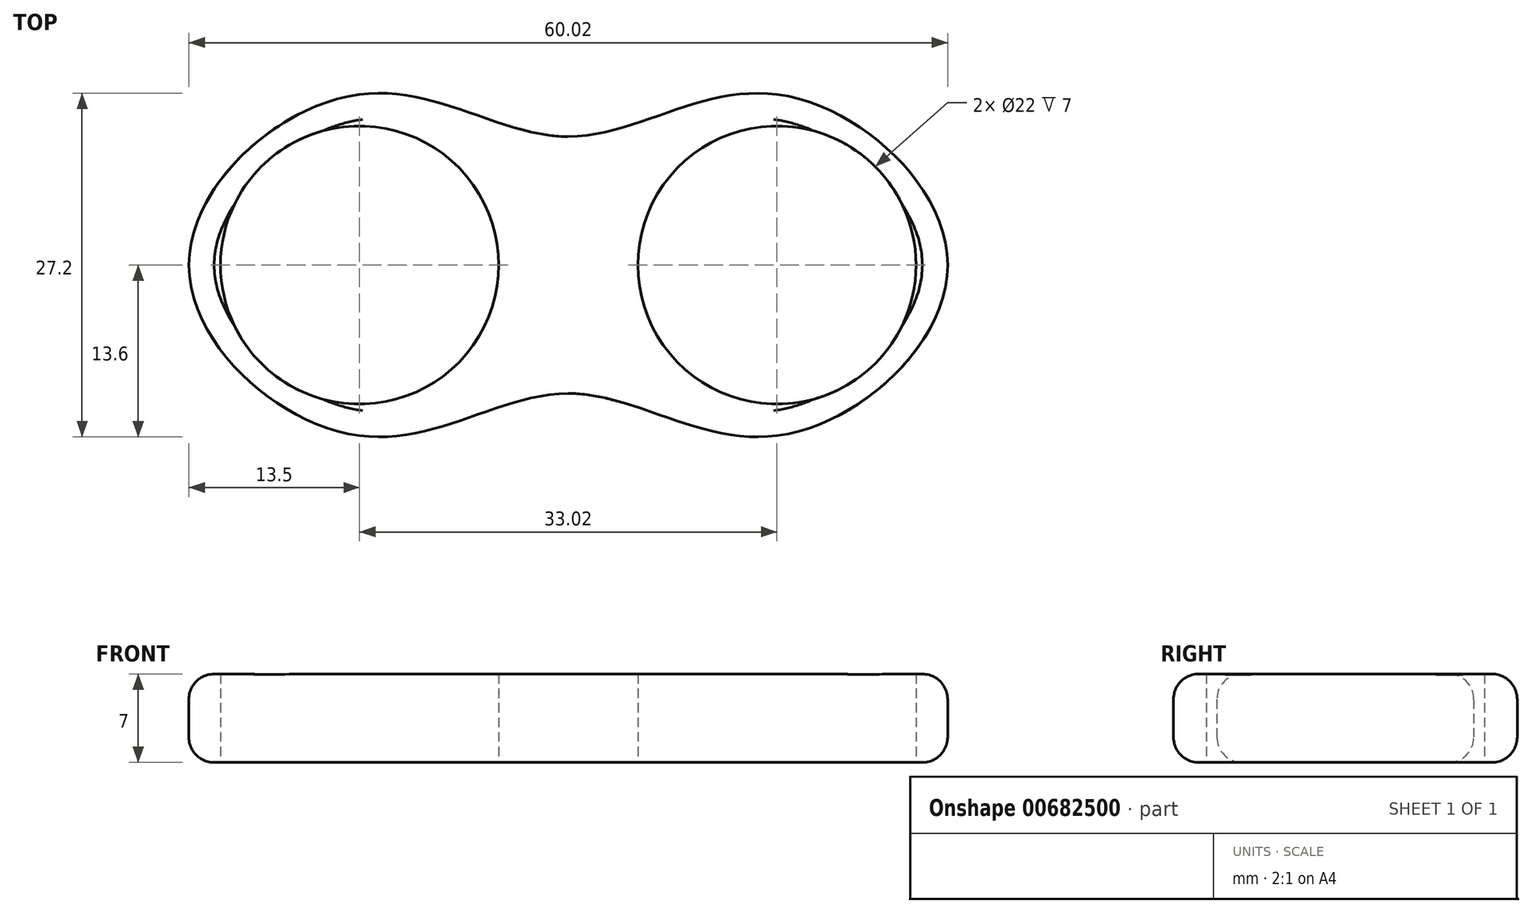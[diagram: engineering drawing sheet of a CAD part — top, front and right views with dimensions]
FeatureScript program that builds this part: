
annotation { "Feature Type Name" : "Feature", "Feature Type Description" : "" }
export const myFeature = defineFeature(function(context is Context, id is Id, definition is map)
    precondition{}
    {
        {
            var Q0;
            Q0=qCreatedBy(makeId("Top.planeOp"),FACE);
            var sketch = newSketch(context, id + "F0", { "sketchPlane" : qUnion([Q0])});
            skLineSegment(sketch, "E0", {"start": v(0, 0) * mm, "end": v(0, 10.16) * mm});
            skLineSegment(sketch, "E1", {"start": v(0, 0) * mm, "end": v(0, -10.16) * mm});
            skLineSegment(sketch, "E2", {"start": v(0, 0) * mm, "end": v(16.51, 0) * mm});
            skLineSegment(sketch, "E3", {"start": v(0, 0) * mm, "end": v(-16.51, 0) * mm});
            skCircle(sketch, "E4", {"center": v(-16.51, 0) * mm, "radius": 11 * mm});
            skCircle(sketch, "E5", {"center": v(16.51, 0) * mm, "radius": 11 * mm});
            skCircle(sketch, "E6", {"center": v(-16.51, 0) * mm, "radius": 13.5 * mm});
            skCircle(sketch, "E7", {"center": v(16.51, 0) * mm, "radius": 13.5 * mm});
            skLineSegment(sketch, "E8", {"start": v(-16.51, 0) * mm, "end": v(-16.51, 13.5) * mm});
            skLineSegment(sketch, "E9", {"start": v(-16.51, 0) * mm, "end": v(-30.01, 0) * mm});
            skLineSegment(sketch, "E10", {"start": v(-16.51, 0) * mm, "end": v(-16.51, -13.5) * mm});
            skLineSegment(sketch, "E11", {"start": v(16.51, 0) * mm, "end": v(16.51, -13.5) * mm});
            skLineSegment(sketch, "E12", {"start": v(16.51, 0) * mm, "end": v(30.01, 0) * mm});
            skLineSegment(sketch, "E13", {"start": v(16.51, 0) * mm, "end": v(16.51, 13.5) * mm});
            skFitSpline(sketch, "E14", {"points": [v(0, 10.16) * mm, v(-16.51, 13.5) * mm, v(-30.01, 0) * mm, v(-16.51, -13.5) * mm, v(0, -10.16) * mm, v(16.51, -13.5) * mm, v(30.01, 0) * mm, v(16.51, 13.5) * mm, v(0, 10.16) * mm]});
            skSolve(sketch);
        }
        {
            var Q0;
            {var subQ0=sQuery(id+"F0.wireOp",EDGE,"E0");Q0=makeQuery(id+"F0.imprint","IMPRINT",FACE,{"disambiguationData":[TD([[makeQuery(id+"F0.imprint","IMPRINT",EDGE,{"derivedFrom":subQ0}),-1.0]])]});}
            var Q1;
            {var subQ0=sQuery(id+"F0.wireOp",EDGE,"E0");Q1=makeQuery(id+"F0.imprint","IMPRINT",FACE,{"disambiguationData":[TD([[makeQuery(id+"F0.imprint","IMPRINT",EDGE,{"derivedFrom":subQ0}),1.0]])]});}
            var Q2;
            {var subQ0=sQuery(id+"F0.wireOp",EDGE,"E1");Q2=makeQuery(id+"F0.imprint","IMPRINT",FACE,{"disambiguationData":[TD([[makeQuery(id+"F0.imprint","IMPRINT",EDGE,{"derivedFrom":subQ0}),-1.0]])]});}
            var Q3;
            {var subQ0=sQuery(id+"F0.wireOp",EDGE,"E1");Q3=makeQuery(id+"F0.imprint","IMPRINT",FACE,{"disambiguationData":[TD([[makeQuery(id+"F0.imprint","IMPRINT",EDGE,{"derivedFrom":subQ0}),1.0]])]});}
            var Q4;
            {var subQ0=sQuery(id+"F0.wireOp",EDGE,"E7");var subQ1=sQuery(id+"F0.wireOp",EDGE,"E2");var subQ2=makeQuery(id+"F0.imprint","INTERSECT",VERTEX,{"derivedFrom":[subQ1,subQ0]});Q4=makeQuery(id+"F0.imprint","IMPRINT",FACE,{"disambiguationData":[TD([[makeQuery(id+"F0.imprint","IMPRINT",EDGE,{"disambiguationData":[TD([[subQ2,-1.0]])],"derivedFrom":subQ1}),-1.0]])]});}
            var Q5;
            {var subQ0=sQuery(id+"F0.wireOp",EDGE,"E7");var subQ1=sQuery(id+"F0.wireOp",EDGE,"E2");var subQ2=makeQuery(id+"F0.imprint","INTERSECT",VERTEX,{"derivedFrom":[subQ1,subQ0]});Q5=makeQuery(id+"F0.imprint","IMPRINT",FACE,{"disambiguationData":[TD([[makeQuery(id+"F0.imprint","IMPRINT",EDGE,{"disambiguationData":[TD([[subQ2,-1.0]])],"derivedFrom":subQ1}),1.0]])]});}
            var Q6;
            {var subQ0=sQuery(id+"F0.wireOp",EDGE,"E6");var subQ1=sQuery(id+"F0.wireOp",EDGE,"E3");var subQ2=makeQuery(id+"F0.imprint","INTERSECT",VERTEX,{"derivedFrom":[subQ1,subQ0]});Q6=makeQuery(id+"F0.imprint","IMPRINT",FACE,{"disambiguationData":[TD([[makeQuery(id+"F0.imprint","IMPRINT",EDGE,{"disambiguationData":[TD([[subQ2,-1.0]])],"derivedFrom":subQ1}),-1.0]])]});}
            var Q7;
            {var subQ0=sQuery(id+"F0.wireOp",EDGE,"E6");var subQ1=sQuery(id+"F0.wireOp",EDGE,"E3");var subQ2=makeQuery(id+"F0.imprint","INTERSECT",VERTEX,{"derivedFrom":[subQ1,subQ0]});Q7=makeQuery(id+"F0.imprint","IMPRINT",FACE,{"disambiguationData":[TD([[makeQuery(id+"F0.imprint","IMPRINT",EDGE,{"disambiguationData":[TD([[subQ2,-1.0]])],"derivedFrom":subQ1}),1.0]])]});}
            var Q8;
            {var subQ0=sQuery(id+"F0.wireOp",EDGE,"E9");var subQ1=sQuery(id+"F0.wireOp",EDGE,"E4");var subQ2=makeQuery(id+"F0.imprint","INTERSECT",VERTEX,{"derivedFrom":[subQ1,subQ0]});Q8=makeQuery(id+"F0.imprint","IMPRINT",FACE,{"disambiguationData":[TD([[makeQuery(id+"F0.imprint","IMPRINT",EDGE,{"disambiguationData":[TD([[subQ2,-1.0]])],"derivedFrom":subQ1}),-1.0]])]});}
            var Q9;
            {var subQ0=sQuery(id+"F0.wireOp",EDGE,"E8");var subQ1=sQuery(id+"F0.wireOp",EDGE,"E4");var subQ2=makeQuery(id+"F0.imprint","INTERSECT",VERTEX,{"derivedFrom":[subQ1,subQ0]});Q9=makeQuery(id+"F0.imprint","IMPRINT",FACE,{"disambiguationData":[TD([[makeQuery(id+"F0.imprint","IMPRINT",EDGE,{"disambiguationData":[TD([[subQ2,-1.0]])],"derivedFrom":subQ1}),-1.0]])]});}
            var Q10;
            {var subQ0=sQuery(id+"F0.wireOp",EDGE,"E13");var subQ1=sQuery(id+"F0.wireOp",EDGE,"E5");var subQ2=makeQuery(id+"F0.imprint","INTERSECT",VERTEX,{"derivedFrom":[subQ1,subQ0]});Q10=makeQuery(id+"F0.imprint","IMPRINT",FACE,{"disambiguationData":[TD([[makeQuery(id+"F0.imprint","IMPRINT",EDGE,{"disambiguationData":[TD([[subQ2,1.0]])],"derivedFrom":subQ1}),-1.0]])]});}
            var Q11;
            {var subQ0=sQuery(id+"F0.wireOp",EDGE,"E12");var subQ1=sQuery(id+"F0.wireOp",EDGE,"E5");var subQ2=makeQuery(id+"F0.imprint","INTERSECT",VERTEX,{"derivedFrom":[subQ1,subQ0]});Q11=makeQuery(id+"F0.imprint","IMPRINT",FACE,{"disambiguationData":[TD([[makeQuery(id+"F0.imprint","IMPRINT",EDGE,{"disambiguationData":[TD([[subQ2,1.0]])],"derivedFrom":subQ1}),-1.0]])]});}
            extrude(context, id + "F1", {"entities" : qUnion([Q0, Q1, Q2, Q3, Q4, Q5, Q6, Q7, Q8, Q9, Q10, Q11]), "depth" : 7 * mm, "offsetDistance" : 25.4 * mm});
        }
        {
            var Q0;
            Q0=makeQuery(id+"F1.opExtrude","CAP_EDGE",EDGE,{"disambiguationData":[OSD([sQuery(id+"F0.wireOp",EDGE,"E14")])],"isStart":false});
            fillet(context, id + "F2", {"entities" : qUnion([Q0]), "radius" : 2 * mm, "tangentPropagation" : true, "allowEdgeOverflow" : false});
        }
        {
            var Q0;
            Q0=makeQuery(id+"F1.opExtrude","CAP_EDGE",EDGE,{"disambiguationData":[OSD([sQuery(id+"F0.wireOp",EDGE,"E14")])],"isStart":true});
            fillet(context, id + "F3", {"entities" : qUnion([Q0]), "radius" : 2 * mm, "tangentPropagation" : true, "allowEdgeOverflow" : false});
        }
    });
